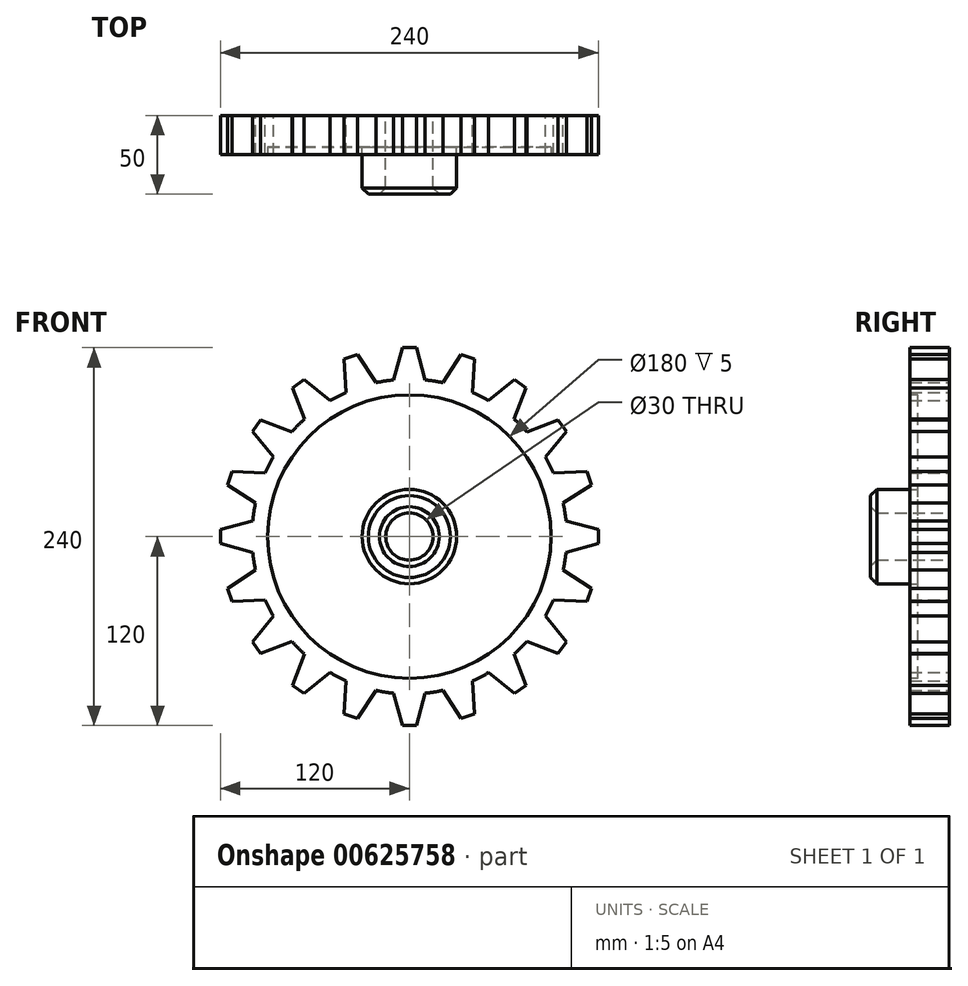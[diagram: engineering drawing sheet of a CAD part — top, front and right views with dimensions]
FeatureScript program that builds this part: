
annotation { "Feature Type Name" : "Feature", "Feature Type Description" : "" }
export const myFeature = defineFeature(function(context is Context, id is Id, definition is map)
    precondition{}
    {
        {
            var Q0;
            Q0=qCreatedBy(makeId("Front.planeOp"),FACE);
            var sketch = newSketch(context, id + "F0", { "sketchPlane" : qUnion([Q0])});
            skCircle(sketch, "E0", {"center": v(0, 0) * mm, "radius": 100 * mm});
            skCircle(sketch, "E1", {"center": v(0, 0) * mm, "radius": 120 * mm, "construction": true});
            skLineSegment(sketch, "E2", {"start": v(-120, 0) * mm, "end": v(-120, 0) * mm});
            skLineSegment(sketch, "E3", {"start": v(-120, 0) * mm, "end": v(-120, -4.5) * mm});
            skLineSegment(sketch, "E4", {"start": v(-120, 0) * mm, "end": v(-120, 4.5) * mm});
            skLineSegment(sketch, "E5", {"start": v(-120, -4.5) * mm, "end": v(-99.5, -10) * mm});
            skLineSegment(sketch, "E6", {"start": v(-120, 4.5) * mm, "end": v(-99.5, 10) * mm});
            skLineSegment(sketch, "E7.1.0", {"start": v(-112.74, -41.36) * mm, "end": v(-91.54, -40.25) * mm});
            skLineSegment(sketch, "E7.1.1", {"start": v(-115.52, -32.8) * mm, "end": v(-97.72, -21.24) * mm});
            skLineSegment(sketch, "E7.1.2", {"start": v(-114.13, -37.08) * mm, "end": v(-115.52, -32.8) * mm});
            skLineSegment(sketch, "E7.1.3", {"start": v(-114.13, -37.08) * mm, "end": v(-112.74, -41.36) * mm});
            skLineSegment(sketch, "E7.2.0", {"start": v(-94.44, -74.17) * mm, "end": v(-74.62, -66.57) * mm});
            skLineSegment(sketch, "E7.2.1", {"start": v(-99.73, -66.9) * mm, "end": v(-86.37, -50.4) * mm});
            skLineSegment(sketch, "E7.2.2", {"start": v(-97.08, -70.53) * mm, "end": v(-99.73, -66.9) * mm});
            skLineSegment(sketch, "E7.2.3", {"start": v(-97.08, -70.53) * mm, "end": v(-94.44, -74.17) * mm});
            skLineSegment(sketch, "E8.1.3.0", {"start": v(-66.9, -99.73) * mm, "end": v(-50.4, -86.37) * mm});
            skLineSegment(sketch, "E8.3.3.0", {"start": v(-74.17, -94.44) * mm, "end": v(-66.57, -74.62) * mm});
            skLineSegment(sketch, "E8.6.3.0", {"start": v(-70.53, -97.08) * mm, "end": v(-74.17, -94.44) * mm});
            skLineSegment(sketch, "E8.9.3.0", {"start": v(-70.53, -97.08) * mm, "end": v(-66.9, -99.73) * mm});
            skLineSegment(sketch, "E8.1.4.0", {"start": v(-32.8, -115.52) * mm, "end": v(-21.24, -97.72) * mm});
            skLineSegment(sketch, "E8.3.4.0", {"start": v(-41.36, -112.74) * mm, "end": v(-40.25, -91.54) * mm});
            skLineSegment(sketch, "E8.6.4.0", {"start": v(-37.08, -114.13) * mm, "end": v(-41.36, -112.74) * mm});
            skLineSegment(sketch, "E8.9.4.0", {"start": v(-37.08, -114.13) * mm, "end": v(-32.8, -115.52) * mm});
            skArc(sketch, "E8.12.4.0", {"start": v(-99.5, -10) * mm, "mid": v(100, 0) * mm, "end": v(-99.5, 10) * mm});
            skLineSegment(sketch, "E8.1.5.0", {"start": v(4.5, -120) * mm, "end": v(10, -99.5) * mm});
            skLineSegment(sketch, "E8.3.5.0", {"start": v(-4.5, -120) * mm, "end": v(-10, -99.5) * mm});
            skLineSegment(sketch, "E8.6.5.0", {"start": v(0, -120) * mm, "end": v(-4.5, -120) * mm});
            skLineSegment(sketch, "E8.9.5.0", {"start": v(0, -120) * mm, "end": v(4.5, -120) * mm});
            skLineSegment(sketch, "E8.1.6.0", {"start": v(41.36, -112.74) * mm, "end": v(40.25, -91.54) * mm});
            skLineSegment(sketch, "E8.3.6.0", {"start": v(32.8, -115.52) * mm, "end": v(21.24, -97.72) * mm});
            skLineSegment(sketch, "E8.6.6.0", {"start": v(37.08, -114.13) * mm, "end": v(32.8, -115.52) * mm});
            skLineSegment(sketch, "E8.9.6.0", {"start": v(37.08, -114.13) * mm, "end": v(41.36, -112.74) * mm});
            skLineSegment(sketch, "E8.1.7.0", {"start": v(74.17, -94.44) * mm, "end": v(66.57, -74.62) * mm});
            skLineSegment(sketch, "E8.3.7.0", {"start": v(66.9, -99.73) * mm, "end": v(50.4, -86.37) * mm});
            skLineSegment(sketch, "E8.6.7.0", {"start": v(70.53, -97.08) * mm, "end": v(66.9, -99.73) * mm});
            skLineSegment(sketch, "E8.9.7.0", {"start": v(70.53, -97.08) * mm, "end": v(74.17, -94.44) * mm});
            skArc(sketch, "E8.12.7.0", {"start": v(-97.72, -21.24) * mm, "mid": v(99.84, 5.7) * mm, "end": v(-99.5, 10) * mm});
            skLineSegment(sketch, "E8.1.8.0", {"start": v(99.73, -66.9) * mm, "end": v(86.37, -50.4) * mm});
            skLineSegment(sketch, "E8.3.8.0", {"start": v(94.44, -74.17) * mm, "end": v(74.62, -66.57) * mm});
            skLineSegment(sketch, "E8.6.8.0", {"start": v(97.08, -70.53) * mm, "end": v(94.44, -74.17) * mm});
            skLineSegment(sketch, "E8.9.8.0", {"start": v(97.08, -70.53) * mm, "end": v(99.73, -66.9) * mm});
            skLineSegment(sketch, "E8.1.9.0", {"start": v(115.52, -32.8) * mm, "end": v(97.72, -21.24) * mm});
            skLineSegment(sketch, "E8.3.9.0", {"start": v(112.74, -41.36) * mm, "end": v(91.54, -40.25) * mm});
            skLineSegment(sketch, "E8.6.9.0", {"start": v(114.13, -37.08) * mm, "end": v(112.74, -41.36) * mm});
            skLineSegment(sketch, "E8.9.9.0", {"start": v(114.13, -37.08) * mm, "end": v(115.52, -32.8) * mm});
            skArc(sketch, "E8.12.9.0", {"start": v(-99.5, -10) * mm, "mid": v(95.1, -30.9) * mm, "end": v(-74.62, 66.57) * mm});
            skLineSegment(sketch, "E8.1.10.0", {"start": v(120, 4.5) * mm, "end": v(99.5, 10) * mm});
            skLineSegment(sketch, "E8.3.10.0", {"start": v(120, -4.5) * mm, "end": v(99.5, -10) * mm});
            skLineSegment(sketch, "E8.6.10.0", {"start": v(120, 0) * mm, "end": v(120, -4.5) * mm});
            skLineSegment(sketch, "E8.9.10.0", {"start": v(120, 0) * mm, "end": v(120, 4.5) * mm});
            skLineSegment(sketch, "E8.1.11.0", {"start": v(112.74, 41.36) * mm, "end": v(91.54, 40.25) * mm});
            skLineSegment(sketch, "E8.3.11.0", {"start": v(115.52, 32.8) * mm, "end": v(97.72, 21.24) * mm});
            skLineSegment(sketch, "E8.6.11.0", {"start": v(114.13, 37.08) * mm, "end": v(115.52, 32.8) * mm});
            skLineSegment(sketch, "E8.9.11.0", {"start": v(114.13, 37.08) * mm, "end": v(112.74, 41.36) * mm});
            skLineSegment(sketch, "E8.1.12.0", {"start": v(94.44, 74.17) * mm, "end": v(74.62, 66.57) * mm});
            skLineSegment(sketch, "E8.3.12.0", {"start": v(99.73, 66.9) * mm, "end": v(86.37, 50.4) * mm});
            skLineSegment(sketch, "E8.6.12.0", {"start": v(97.08, 70.53) * mm, "end": v(99.73, 66.9) * mm});
            skLineSegment(sketch, "E8.9.12.0", {"start": v(97.08, 70.53) * mm, "end": v(94.44, 74.17) * mm});
            skArc(sketch, "E8.12.12.0", {"start": v(-99.5, -10) * mm, "mid": v(100, 0) * mm, "end": v(-99.5, 10) * mm});
            skLineSegment(sketch, "E8.1.13.0", {"start": v(66.9, 99.73) * mm, "end": v(50.4, 86.37) * mm});
            skLineSegment(sketch, "E8.3.13.0", {"start": v(74.17, 94.44) * mm, "end": v(66.57, 74.62) * mm});
            skLineSegment(sketch, "E8.6.13.0", {"start": v(70.53, 97.08) * mm, "end": v(74.17, 94.44) * mm});
            skLineSegment(sketch, "E8.9.13.0", {"start": v(70.53, 97.08) * mm, "end": v(66.9, 99.73) * mm});
            skLineSegment(sketch, "E8.1.14.0", {"start": v(32.8, 115.52) * mm, "end": v(21.24, 97.72) * mm});
            skLineSegment(sketch, "E8.3.14.0", {"start": v(41.36, 112.74) * mm, "end": v(40.25, 91.54) * mm});
            skLineSegment(sketch, "E8.6.14.0", {"start": v(37.08, 114.13) * mm, "end": v(41.36, 112.74) * mm});
            skLineSegment(sketch, "E8.9.14.0", {"start": v(37.08, 114.13) * mm, "end": v(32.8, 115.52) * mm});
            skLineSegment(sketch, "E8.1.15.0", {"start": v(-4.5, 120) * mm, "end": v(-10, 99.5) * mm});
            skLineSegment(sketch, "E8.3.15.0", {"start": v(4.5, 120) * mm, "end": v(10, 99.5) * mm});
            skLineSegment(sketch, "E8.6.15.0", {"start": v(0, 120) * mm, "end": v(4.5, 120) * mm});
            skLineSegment(sketch, "E8.9.15.0", {"start": v(0, 120) * mm, "end": v(-4.5, 120) * mm});
            skLineSegment(sketch, "E8.1.16.0", {"start": v(-41.36, 112.74) * mm, "end": v(-40.25, 91.54) * mm});
            skLineSegment(sketch, "E8.3.16.0", {"start": v(-32.8, 115.52) * mm, "end": v(-21.24, 97.72) * mm});
            skLineSegment(sketch, "E8.6.16.0", {"start": v(-37.08, 114.13) * mm, "end": v(-32.8, 115.52) * mm});
            skLineSegment(sketch, "E8.9.16.0", {"start": v(-37.08, 114.13) * mm, "end": v(-41.36, 112.74) * mm});
            skLineSegment(sketch, "E8.1.17.0", {"start": v(-74.17, 94.44) * mm, "end": v(-66.57, 74.62) * mm});
            skLineSegment(sketch, "E8.3.17.0", {"start": v(-66.9, 99.73) * mm, "end": v(-50.4, 86.37) * mm});
            skLineSegment(sketch, "E8.6.17.0", {"start": v(-70.53, 97.08) * mm, "end": v(-66.9, 99.73) * mm});
            skLineSegment(sketch, "E8.9.17.0", {"start": v(-70.53, 97.08) * mm, "end": v(-74.17, 94.44) * mm});
            skLineSegment(sketch, "E8.1.18.0", {"start": v(-99.73, 66.9) * mm, "end": v(-86.37, 50.4) * mm});
            skLineSegment(sketch, "E8.3.18.0", {"start": v(-94.44, 74.17) * mm, "end": v(-74.62, 66.57) * mm});
            skLineSegment(sketch, "E8.6.18.0", {"start": v(-97.08, 70.53) * mm, "end": v(-94.44, 74.17) * mm});
            skLineSegment(sketch, "E8.9.18.0", {"start": v(-97.08, 70.53) * mm, "end": v(-99.73, 66.9) * mm});
            skLineSegment(sketch, "E8.1.19.0", {"start": v(-115.52, 32.8) * mm, "end": v(-97.72, 21.24) * mm});
            skLineSegment(sketch, "E8.3.19.0", {"start": v(-112.74, 41.36) * mm, "end": v(-91.54, 40.25) * mm});
            skLineSegment(sketch, "E8.6.19.0", {"start": v(-114.13, 37.08) * mm, "end": v(-112.74, 41.36) * mm});
            skLineSegment(sketch, "E8.9.19.0", {"start": v(-114.13, 37.08) * mm, "end": v(-115.52, 32.8) * mm});
            skArc(sketch, "E9.trimOffspring", {"start": v(-97.72, 21.24) * mm, "mid": v(-98.77, 15.64) * mm, "end": v(-99.5, 10) * mm});
            skSolve(sketch);
        }
        {
            var Q0;
            {var subQ0=sQuery(id+"F0.wireOp",EDGE,"E0");var subQ18=makeQuery(id+"F0.imprint","INTERSECT",VERTEX,{"derivedFrom":[sQuery(id+"F0.wireOp",EDGE,"E8.1.9.0"),subQ0]});Q0=makeQuery(id+"F0.imprint","IMPRINT",FACE,{"disambiguationData":[TD([[makeQuery(id+"F0.imprint","IMPRINT",EDGE,{"disambiguationData":[TD([[subQ18,-1.0]])],"derivedFrom":subQ0}),1.0]])]});}
            var Q1;
            Q1=makeQuery(id+"F0.imprint","IMPRINT",FACE,{"disambiguationData":[TD([[makeQuery(id+"F0.imprint","IMPRINT",EDGE,{"derivedFrom":sQuery(id+"F0.wireOp",EDGE,"E3")}),1.0]])]});
            var Q2;
            {var subQ2=sQuery(id+"F0.wireOp",EDGE,"E8.1.19.0");Q2=makeQuery(id+"F0.imprint","IMPRINT",FACE,{"disambiguationData":[TD([[makeQuery(id+"F0.imprint","IMPRINT",EDGE,{"derivedFrom":subQ2}),1.0]])]});}
            var Q3;
            {var subQ1=sQuery(id+"F0.wireOp",EDGE,"E8.1.18.0");Q3=makeQuery(id+"F0.imprint","IMPRINT",FACE,{"disambiguationData":[TD([[makeQuery(id+"F0.imprint","IMPRINT",EDGE,{"derivedFrom":subQ1}),1.0]])]});}
            var Q4;
            {var subQ1=sQuery(id+"F0.wireOp",EDGE,"E8.1.17.0");Q4=makeQuery(id+"F0.imprint","IMPRINT",FACE,{"disambiguationData":[TD([[makeQuery(id+"F0.imprint","IMPRINT",EDGE,{"derivedFrom":subQ1}),1.0]])]});}
            var Q5;
            {var subQ1=sQuery(id+"F0.wireOp",EDGE,"E8.1.16.0");Q5=makeQuery(id+"F0.imprint","IMPRINT",FACE,{"disambiguationData":[TD([[makeQuery(id+"F0.imprint","IMPRINT",EDGE,{"derivedFrom":subQ1}),1.0]])]});}
            var Q6;
            {var subQ1=sQuery(id+"F0.wireOp",EDGE,"E8.1.15.0");Q6=makeQuery(id+"F0.imprint","IMPRINT",FACE,{"disambiguationData":[TD([[makeQuery(id+"F0.imprint","IMPRINT",EDGE,{"derivedFrom":subQ1}),1.0]])]});}
            var Q7;
            {var subQ1=sQuery(id+"F0.wireOp",EDGE,"E8.1.14.0");Q7=makeQuery(id+"F0.imprint","IMPRINT",FACE,{"disambiguationData":[TD([[makeQuery(id+"F0.imprint","IMPRINT",EDGE,{"derivedFrom":subQ1}),1.0]])]});}
            var Q8;
            {var subQ1=sQuery(id+"F0.wireOp",EDGE,"E8.1.13.0");Q8=makeQuery(id+"F0.imprint","IMPRINT",FACE,{"disambiguationData":[TD([[makeQuery(id+"F0.imprint","IMPRINT",EDGE,{"derivedFrom":subQ1}),1.0]])]});}
            var Q9;
            {var subQ1=sQuery(id+"F0.wireOp",EDGE,"E8.1.12.0");Q9=makeQuery(id+"F0.imprint","IMPRINT",FACE,{"disambiguationData":[TD([[makeQuery(id+"F0.imprint","IMPRINT",EDGE,{"derivedFrom":subQ1}),1.0]])]});}
            var Q10;
            {var subQ1=sQuery(id+"F0.wireOp",EDGE,"E8.1.11.0");Q10=makeQuery(id+"F0.imprint","IMPRINT",FACE,{"disambiguationData":[TD([[makeQuery(id+"F0.imprint","IMPRINT",EDGE,{"derivedFrom":subQ1}),1.0]])]});}
            var Q11;
            {var subQ1=sQuery(id+"F0.wireOp",EDGE,"E8.1.10.0");Q11=makeQuery(id+"F0.imprint","IMPRINT",FACE,{"disambiguationData":[TD([[makeQuery(id+"F0.imprint","IMPRINT",EDGE,{"derivedFrom":subQ1}),1.0]])]});}
            var Q12;
            {var subQ1=sQuery(id+"F0.wireOp",EDGE,"E8.1.9.0");Q12=makeQuery(id+"F0.imprint","IMPRINT",FACE,{"disambiguationData":[TD([[makeQuery(id+"F0.imprint","IMPRINT",EDGE,{"derivedFrom":subQ1}),1.0]])]});}
            var Q13;
            {var subQ1=sQuery(id+"F0.wireOp",EDGE,"E8.1.8.0");Q13=makeQuery(id+"F0.imprint","IMPRINT",FACE,{"disambiguationData":[TD([[makeQuery(id+"F0.imprint","IMPRINT",EDGE,{"derivedFrom":subQ1}),1.0]])]});}
            var Q14;
            {var subQ1=sQuery(id+"F0.wireOp",EDGE,"E8.1.7.0");Q14=makeQuery(id+"F0.imprint","IMPRINT",FACE,{"disambiguationData":[TD([[makeQuery(id+"F0.imprint","IMPRINT",EDGE,{"derivedFrom":subQ1}),1.0]])]});}
            var Q15;
            {var subQ2=sQuery(id+"F0.wireOp",EDGE,"E8.1.6.0");Q15=makeQuery(id+"F0.imprint","IMPRINT",FACE,{"disambiguationData":[TD([[makeQuery(id+"F0.imprint","IMPRINT",EDGE,{"derivedFrom":subQ2}),1.0]])]});}
            var Q16;
            {var subQ1=sQuery(id+"F0.wireOp",EDGE,"E8.1.5.0");Q16=makeQuery(id+"F0.imprint","IMPRINT",FACE,{"disambiguationData":[TD([[makeQuery(id+"F0.imprint","IMPRINT",EDGE,{"derivedFrom":subQ1}),1.0]])]});}
            var Q17;
            {var subQ1=sQuery(id+"F0.wireOp",EDGE,"E8.1.4.0");Q17=makeQuery(id+"F0.imprint","IMPRINT",FACE,{"disambiguationData":[TD([[makeQuery(id+"F0.imprint","IMPRINT",EDGE,{"derivedFrom":subQ1}),1.0]])]});}
            var Q18;
            {var subQ1=sQuery(id+"F0.wireOp",EDGE,"E8.1.3.0");Q18=makeQuery(id+"F0.imprint","IMPRINT",FACE,{"disambiguationData":[TD([[makeQuery(id+"F0.imprint","IMPRINT",EDGE,{"derivedFrom":subQ1}),1.0]])]});}
            var Q19;
            {var subQ1=sQuery(id+"F0.wireOp",EDGE,"E7.2.0");Q19=makeQuery(id+"F0.imprint","IMPRINT",FACE,{"disambiguationData":[TD([[makeQuery(id+"F0.imprint","IMPRINT",EDGE,{"derivedFrom":subQ1}),1.0]])]});}
            var Q20;
            {var subQ1=sQuery(id+"F0.wireOp",EDGE,"E7.1.0");Q20=makeQuery(id+"F0.imprint","IMPRINT",FACE,{"disambiguationData":[TD([[makeQuery(id+"F0.imprint","IMPRINT",EDGE,{"derivedFrom":subQ1}),1.0]])]});}
            extrude(context, id + "F1", {"entities" : qUnion([Q0, Q1, Q2, Q3, Q4, Q5, Q6, Q7, Q8, Q9, Q10, Q11, Q12, Q13, Q14, Q15, Q16, Q17, Q18, Q19, Q20]), "depth" : 25 * mm, "offsetDistance" : 25 * mm});
        }
        {
            var Q0;
            Q0=makeQuery(id+"F1.opExtrude","CAP_FACE",FACE,{"disambiguationData":[OSD([sQuery(id+"F0.wireOp",EDGE,"E3"),sQuery(id+"F0.wireOp",EDGE,"E4"),sQuery(id+"F0.wireOp",EDGE,"E5"),sQuery(id+"F0.wireOp",EDGE,"E6"),sQuery(id+"F0.wireOp",EDGE,"E7.1.0"),sQuery(id+"F0.wireOp",EDGE,"E7.1.1"),sQuery(id+"F0.wireOp",EDGE,"E7.1.2"),sQuery(id+"F0.wireOp",EDGE,"E7.1.3"),sQuery(id+"F0.wireOp",EDGE,"E7.2.0"),sQuery(id+"F0.wireOp",EDGE,"E7.2.1"),sQuery(id+"F0.wireOp",EDGE,"E7.2.2"),sQuery(id+"F0.wireOp",EDGE,"E7.2.3"),sQuery(id+"F0.wireOp",EDGE,"E8.1.3.0"),sQuery(id+"F0.wireOp",EDGE,"E8.3.3.0"),sQuery(id+"F0.wireOp",EDGE,"E8.6.3.0"),sQuery(id+"F0.wireOp",EDGE,"E8.9.3.0"),sQuery(id+"F0.wireOp",EDGE,"E8.1.4.0"),sQuery(id+"F0.wireOp",EDGE,"E8.3.4.0"),sQuery(id+"F0.wireOp",EDGE,"E8.6.4.0"),sQuery(id+"F0.wireOp",EDGE,"E8.9.4.0"),sQuery(id+"F0.wireOp",EDGE,"E8.1.5.0"),sQuery(id+"F0.wireOp",EDGE,"E8.3.5.0"),sQuery(id+"F0.wireOp",EDGE,"E8.6.5.0"),sQuery(id+"F0.wireOp",EDGE,"E8.9.5.0"),sQuery(id+"F0.wireOp",EDGE,"E8.1.6.0"),sQuery(id+"F0.wireOp",EDGE,"E8.3.6.0"),sQuery(id+"F0.wireOp",EDGE,"E8.6.6.0"),sQuery(id+"F0.wireOp",EDGE,"E8.9.6.0"),sQuery(id+"F0.wireOp",EDGE,"E8.1.7.0"),sQuery(id+"F0.wireOp",EDGE,"E8.3.7.0"),sQuery(id+"F0.wireOp",EDGE,"E8.6.7.0"),sQuery(id+"F0.wireOp",EDGE,"E8.9.7.0"),sQuery(id+"F0.wireOp",EDGE,"E8.1.8.0"),sQuery(id+"F0.wireOp",EDGE,"E8.3.8.0"),sQuery(id+"F0.wireOp",EDGE,"E8.6.8.0"),sQuery(id+"F0.wireOp",EDGE,"E8.9.8.0"),sQuery(id+"F0.wireOp",EDGE,"E8.1.9.0"),sQuery(id+"F0.wireOp",EDGE,"E8.3.9.0"),sQuery(id+"F0.wireOp",EDGE,"E8.6.9.0"),sQuery(id+"F0.wireOp",EDGE,"E8.9.9.0"),sQuery(id+"F0.wireOp",EDGE,"E8.1.10.0"),sQuery(id+"F0.wireOp",EDGE,"E8.3.10.0"),sQuery(id+"F0.wireOp",EDGE,"E8.6.10.0"),sQuery(id+"F0.wireOp",EDGE,"E8.9.10.0"),sQuery(id+"F0.wireOp",EDGE,"E8.1.11.0"),sQuery(id+"F0.wireOp",EDGE,"E8.3.11.0"),sQuery(id+"F0.wireOp",EDGE,"E8.6.11.0"),sQuery(id+"F0.wireOp",EDGE,"E8.9.11.0"),sQuery(id+"F0.wireOp",EDGE,"E8.1.12.0"),sQuery(id+"F0.wireOp",EDGE,"E8.3.12.0"),sQuery(id+"F0.wireOp",EDGE,"E8.6.12.0"),sQuery(id+"F0.wireOp",EDGE,"E8.9.12.0"),sQuery(id+"F0.wireOp",EDGE,"E8.1.13.0"),sQuery(id+"F0.wireOp",EDGE,"E8.3.13.0"),sQuery(id+"F0.wireOp",EDGE,"E8.6.13.0"),sQuery(id+"F0.wireOp",EDGE,"E8.9.13.0"),sQuery(id+"F0.wireOp",EDGE,"E8.1.14.0"),sQuery(id+"F0.wireOp",EDGE,"E8.3.14.0"),sQuery(id+"F0.wireOp",EDGE,"E8.6.14.0"),sQuery(id+"F0.wireOp",EDGE,"E8.9.14.0"),sQuery(id+"F0.wireOp",EDGE,"E8.1.15.0"),sQuery(id+"F0.wireOp",EDGE,"E8.3.15.0"),sQuery(id+"F0.wireOp",EDGE,"E8.6.15.0"),sQuery(id+"F0.wireOp",EDGE,"E8.9.15.0"),sQuery(id+"F0.wireOp",EDGE,"E8.1.16.0"),sQuery(id+"F0.wireOp",EDGE,"E8.3.16.0"),sQuery(id+"F0.wireOp",EDGE,"E8.6.16.0"),sQuery(id+"F0.wireOp",EDGE,"E8.9.16.0"),sQuery(id+"F0.wireOp",EDGE,"E8.1.17.0"),sQuery(id+"F0.wireOp",EDGE,"E8.3.17.0"),sQuery(id+"F0.wireOp",EDGE,"E8.6.17.0"),sQuery(id+"F0.wireOp",EDGE,"E8.9.17.0"),sQuery(id+"F0.wireOp",EDGE,"E8.1.18.0"),sQuery(id+"F0.wireOp",EDGE,"E8.3.18.0"),sQuery(id+"F0.wireOp",EDGE,"E8.6.18.0"),sQuery(id+"F0.wireOp",EDGE,"E8.9.18.0"),sQuery(id+"F0.wireOp",EDGE,"E8.1.19.0"),sQuery(id+"F0.wireOp",EDGE,"E8.3.19.0"),sQuery(id+"F0.wireOp",EDGE,"E8.6.19.0"),sQuery(id+"F0.wireOp",EDGE,"E8.9.19.0"),sQuery(id+"F0.wireOp",EDGE,"E0")])],"isStart":false});
            var sketch = newSketch(context, id + "F2", { "sketchPlane" : qUnion([Q0])});
            skCircle(sketch, "E10", {"center": v(0, 0) * mm, "radius": 90 * mm});
            skSolve(sketch);
        }
        {
            var Q0;
            Q0=makeQuery(id+"F2.imprint","IMPRINT",FACE,{"disambiguationData":[TD([[makeQuery(id+"F2.imprint","IMPRINT",EDGE,{"derivedFrom":sQuery(id+"F2.wireOp",EDGE,"E10")}),1.0]])]});
            extrude(context, id + "F3", {"entities" : qUnion([Q0]), "operationType" : NewBodyOperationType.REMOVE, "oppositeDirection" : true, "depth" : 5 * mm, "offsetDistance" : 25 * mm});
        }
        {
            var Q0;
            Q0=makeQuery(id+"F3.boolean.opBoolean","COPY",FACE,{"derivedFrom":makeQuery(id+"F3.opExtrude","CAP_FACE",FACE,{"disambiguationData":[OSD([sQuery(id+"F2.wireOp",EDGE,"E10")])],"isStart":false})});
            var sketch = newSketch(context, id + "F4", { "sketchPlane" : qUnion([Q0])});
            skCircle(sketch, "E11", {"center": v(0, 0) * mm, "radius": 30 * mm});
            skCircle(sketch, "E12", {"center": v(0, 0) * mm, "radius": 15 * mm});
            skSolve(sketch);
        }
        {
            var Q0;
            Q0=makeQuery(id+"F4.imprint","IMPRINT",FACE,{"disambiguationData":[TD([[makeQuery(id+"F4.imprint","IMPRINT",EDGE,{"derivedFrom":sQuery(id+"F4.wireOp",EDGE,"E11")}),1.0]])]});
            extrude(context, id + "F5", {"entities" : qUnion([Q0]), "operationType" : NewBodyOperationType.ADD, "depth" : 30 * mm, "offsetDistance" : 25 * mm});
        }
        {
            var Q0;
            Q0=makeQuery(id+"F5.boolean.opBoolean","SPLIT",FACE,{"disambiguationData":[TD([makeQuery(id+"F5.opExtrude","SWEPT_FACE",FACE,{"disambiguationData":[OSD([sQuery(id+"F4.wireOp",EDGE,"E12")])]})])],"derivedFrom":makeQuery(id+"F3.boolean.opBoolean","COPY",FACE,{"derivedFrom":makeQuery(id+"F3.opExtrude","CAP_FACE",FACE,{"disambiguationData":[OSD([sQuery(id+"F2.wireOp",EDGE,"E10")])],"isStart":false})})});
            extrude(context, id + "F6", {"entities" : qUnion([Q0]), "operationType" : NewBodyOperationType.REMOVE, "oppositeDirection" : true, "depth" : 100 * mm, "offsetDistance" : 25 * mm});
        }
        {
            var Q0;
            Q0=makeQuery(id+"F5.opExtrude","CAP_FACE",FACE,{"disambiguationData":[OSD([sQuery(id+"F4.wireOp",EDGE,"E11"),sQuery(id+"F4.wireOp",EDGE,"E12")])],"isStart":false});
            chamfer(context, id + "F7", {"entities" : qUnion([Q0]), "width" : 4 * mm, "tangentPropagation" : true});
        }
    });
